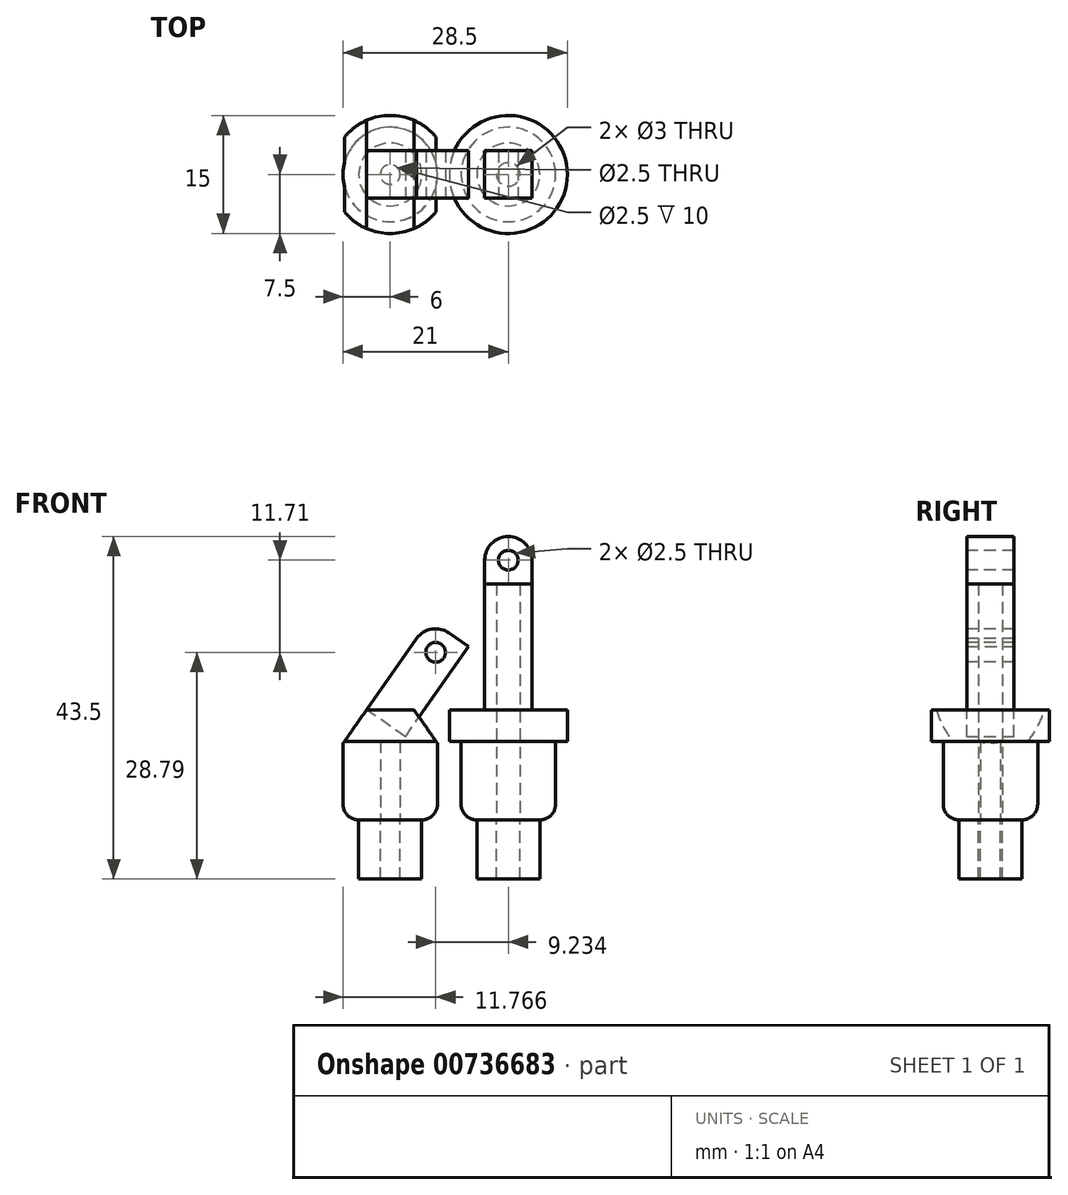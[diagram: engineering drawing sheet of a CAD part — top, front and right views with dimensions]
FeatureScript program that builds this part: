
annotation { "Feature Type Name" : "Feature", "Feature Type Description" : "" }
export const myFeature = defineFeature(function(context is Context, id is Id, definition is map)
    precondition{}
    {
        {
            var Q0;
            Q0=qCreatedBy(makeId("Top.planeOp"),FACE);
            var sketch = newSketch(context, id + "F0", { "sketchPlane" : qUnion([Q0])});
            skCircle(sketch, "E0", {"center": v(0, 0) * mm, "radius": 6 * mm});
            skCircle(sketch, "E1", {"center": v(15, 0) * mm, "radius": 6 * mm});
            skCircle(sketch, "E2", {"center": v(15, 0) * mm, "radius": 1.5 * mm});
            skSolve(sketch);
        }
        {
            var Q0;
            Q0=makeQuery(id+"F0.imprint","IMPRINT",FACE,{"disambiguationData":[TD([[makeQuery(id+"F0.imprint","IMPRINT",EDGE,{"derivedFrom":sQuery(id+"F0.wireOp",EDGE,"E0")}),1.0]])]});
            extrude(context, id + "F1", {"entities" : qUnion([Q0]), "depth" : 10 * mm, "offsetDistance" : 25 * mm});
        }
        {
            var Q0;
            Q0=makeQuery(id+"F1.opExtrude","CAP_FACE",FACE,{"disambiguationData":[OSD([sQuery(id+"F0.wireOp",EDGE,"E0")])],"isStart":false});
            var sketch = newSketch(context, id + "F2", { "sketchPlane" : qUnion([Q0])});
            skCircle(sketch, "E3", {"center": v(0, 0) * mm, "radius": 7.5 * mm});
            skSolve(sketch);
        }
        {
            var Q0;
            Q0 = qSketchRegion(id + "F2", true);
            extrude(context, id + "F3", {"entities" : qUnion([Q0]), "operationType" : NewBodyOperationType.ADD, "depth" : 4 * mm, "offsetDistance" : 25 * mm});
        }
        {
            var Q0;
            Q0=makeQuery(id+"F3.opExtrude","CAP_FACE",FACE,{"disambiguationData":[OSD([sQuery(id+"F2.wireOp",EDGE,"E3")])],"isStart":false});
            var sketch = newSketch(context, id + "F4", { "sketchPlane" : qUnion([Q0])});
            skLineSegment(sketch, "E4.bottom", {"start": v(3, 6.87) * mm, "end": v(10, 6.87) * mm});
            skLineSegment(sketch, "E4.top", {"start": v(3, -6.87) * mm, "end": v(10, -6.87) * mm});
            skLineSegment(sketch, "E4.right", {"start": v(10, 6.87) * mm, "end": v(10, -6.87) * mm});
            skLineSegment(sketch, "E5.bottom", {"start": v(-3, 6.87) * mm, "end": v(-10, 6.87) * mm});
            skLineSegment(sketch, "E5.top", {"start": v(-3, -6.87) * mm, "end": v(-10, -6.87) * mm});
            skLineSegment(sketch, "E5.left", {"start": v(-3, 6.87) * mm, "end": v(-3, -6.87) * mm});
            skLineSegment(sketch, "E5.right", {"start": v(-10, 6.87) * mm, "end": v(-10, -6.87) * mm});
            skLineSegment(sketch, "E6", {"start": v(3, -6.87) * mm, "end": v(3, 6.87) * mm});
            skLineSegment(sketch, "E7.top", {"start": v(-3, -3) * mm, "end": v(3, -3) * mm});
            skLineSegment(sketch, "E7.left", {"start": v(-3, 0) * mm, "end": v(-3, -3) * mm});
            skLineSegment(sketch, "E7.right", {"start": v(3, 3) * mm, "end": v(3, -3) * mm});
            skLineSegment(sketch, "E8", {"start": v(3, 3) * mm, "end": v(-3, 3) * mm});
            skLineSegment(sketch, "E9", {"start": v(-3, 3) * mm, "end": v(-3, 0) * mm});
            skSolve(sketch);
        }
        {
            var Q0;
            {var subQ0=sQuery(id+"F4.wireOp",EDGE,"E5.bottom");Q0=makeQuery(id+"F4.imprint","IMPRINT",FACE,{"disambiguationData":[TD([[makeQuery(id+"F4.imprint","IMPRINT",EDGE,{"derivedFrom":subQ0}),1.0]])]});}
            var Q1;
            {var subQ0=sQuery(id+"F4.wireOp",EDGE,"E5.left");var subQ1=makeQuery(id+"F4.imprint","INTERSECT",VERTEX,{"derivedFrom":[sQuery(id+"F4.wireOp",EDGE,"yuGE9SbZ-14rk-lHCZ-kvU9-YbVtqfjyu9ov.bottom"),subQ0]});Q1=makeQuery(id+"F4.imprint","IMPRINT",FACE,{"disambiguationData":[TD([[makeQuery(id+"F4.imprint","IMPRINT",EDGE,{"disambiguationData":[TD([[subQ1,-1.0]])],"derivedFrom":subQ0}),-1.0]])]});}
            var Q2;
            Q2=sQuery(id+"F4.wireOp",EDGE,"E5.left");
            revolve(context, id + "F5", {"operationType" : NewBodyOperationType.REMOVE, "surfaceOperationType" : NewSurfaceOperationType.NEW, "entities" : qUnion([Q0, Q1]), "axis" : qUnion([Q2]), "revolveType" : RevolveType.ONE_DIRECTION, "angle" : 55 * degree});
        }
        {
            var Q0;
            {var subQ0=sQuery(id+"F4.wireOp",EDGE,"E6");Q0=makeQuery(id+"F4.imprint","IMPRINT",FACE,{"disambiguationData":[TD([[makeQuery(id+"F4.imprint","IMPRINT",EDGE,{"derivedFrom":subQ0}),-1.0]])]});}
            var Q1;
            {var subQ0=sQuery(id+"F4.wireOp",EDGE,"E4.bottom");Q1=makeQuery(id+"F4.imprint","IMPRINT",FACE,{"disambiguationData":[TD([[makeQuery(id+"F4.imprint","IMPRINT",EDGE,{"derivedFrom":subQ0}),-1.0]])]});}
            var Q2;
            Q2=sQuery(id+"F4.wireOp",EDGE,"E6");
            revolve(context, id + "F6", {"operationType" : NewBodyOperationType.REMOVE, "surfaceOperationType" : NewSurfaceOperationType.NEW, "entities" : qUnion([Q0, Q1]), "axis" : qUnion([Q2]), "revolveType" : RevolveType.ONE_DIRECTION, "angle" : 55 * degree});
        }
        {
            var Q0;
            Q0=makeQuery(id+"F1.opExtrude","CAP_FACE",FACE,{"disambiguationData":[OSD([sQuery(id+"F0.wireOp",EDGE,"E0")])],"isStart":true});
            var sketch = newSketch(context, id + "F7", { "sketchPlane" : qUnion([Q0])});
            skCircle(sketch, "E10", {"center": v(0, 0) * mm, "radius": 1.25 * mm});
            skSolve(sketch);
        }
        {
            var Q0;
            Q0 = qSketchRegion(id + "F7", true);
            extrude(context, id + "F8", {"entities" : qUnion([Q0]), "operationType" : NewBodyOperationType.REMOVE, "oppositeDirection" : true, "depth" : 10 * mm, "offsetDistance" : 25 * mm});
        }
        {
            var Q0;
            Q0=makeQuery(id+"F1.opExtrude","CAP_EDGE",EDGE,{"disambiguationData":[OSD([sQuery(id+"F0.wireOp",EDGE,"E0")])],"isStart":true});
            fillet(context, id + "F9", {"entities" : qUnion([Q0]), "radius" : 2 * mm, "tangentPropagation" : true, "allowEdgeOverflow" : false});
        }
        {
            var Q0;
            Q0=makeQuery(id+"F0.imprint","IMPRINT",FACE,{"disambiguationData":[TD([[makeQuery(id+"F0.imprint","IMPRINT",EDGE,{"derivedFrom":sQuery(id+"F0.wireOp",EDGE,"E1")}),1.0]])]});
            extrude(context, id + "F10", {"entities" : qUnion([Q0]), "depth" : 10 * mm, "offsetDistance" : 25 * mm});
        }
        {
            var Q0;
            Q0=makeQuery(id+"F10.opExtrude","CAP_FACE",FACE,{"disambiguationData":[OSD([sQuery(id+"F0.wireOp",EDGE,"E1")])],"isStart":false});
            var sketch = newSketch(context, id + "F11", { "sketchPlane" : qUnion([Q0])});
            skCircle(sketch, "E11", {"center": v(15, 0) * mm, "radius": 7.5 * mm});
            skSolve(sketch);
        }
        {
            var Q0;
            Q0 = qSketchRegion(id + "F11", true);
            extrude(context, id + "F12", {"entities" : qUnion([Q0]), "operationType" : NewBodyOperationType.ADD, "depth" : 4 * mm, "offsetDistance" : 25 * mm});
        }
        {
            var Q0;
            Q0=makeQuery(id+"F10.opExtrude","CAP_EDGE",EDGE,{"disambiguationData":[OSD([sQuery(id+"F0.wireOp",EDGE,"E1")])],"isStart":true});
            fillet(context, id + "F13", {"entities" : qUnion([Q0]), "radius" : 2 * mm, "tangentPropagation" : true, "allowEdgeOverflow" : false});
        }
        {
            var Q0;
            Q0=makeQuery(id+"F12.boolean.opBoolean","SPLIT",FACE,{"disambiguationData":[TD([makeQuery(id+"F10.opExtrude","SWEPT_FACE",FACE,{"disambiguationData":[OSD([sQuery(id+"F0.wireOp",EDGE,"E2")])]})])],"derivedFrom":makeQuery(id+"F12.opExtrude","CAP_FACE",FACE,{"disambiguationData":[OSD([sQuery(id+"F11.wireOp",EDGE,"E11")])],"isStart":true})});
            extrude(context, id + "F14", {"entities" : qUnion([Q0]), "operationType" : NewBodyOperationType.REMOVE, "oppositeDirection" : true, "depth" : 25 * mm, "offsetDistance" : 25 * mm});
        }
        {
            var Q0;
            Q0=makeQuery(id+"F5.boolean.opBoolean","COPY",FACE,{"derivedFrom":makeQuery(id+"F5.opRevolve","CAP_FACE",FACE,{"disambiguationData":[OSD([sQuery(id+"F4.wireOp",EDGE,"E5.bottom"),sQuery(id+"F4.wireOp",EDGE,"E5.top"),sQuery(id+"F4.wireOp",EDGE,"E5.left"),sQuery(id+"F4.wireOp",EDGE,"E5.right"),sQuery(id+"F4.wireOp",EDGE,"E7.left"),sQuery(id+"F4.wireOp",EDGE,"E9")])],"isStart":false})});
            var sketch = newSketch(context, id + "F15", { "sketchPlane" : qUnion([Q0])});
            skLineSegment(sketch, "E12.bottom", {"start": v(3, 9.75) * mm, "end": v(-3, 9.75) * mm});
            skLineSegment(sketch, "E12.top", {"start": v(3, 23.75) * mm, "end": v(-3, 23.75) * mm});
            skLineSegment(sketch, "E12.left", {"start": v(3, 9.75) * mm, "end": v(3, 23.75) * mm});
            skLineSegment(sketch, "E12.right", {"start": v(-3, 9.75) * mm, "end": v(-3, 23.75) * mm});
            skSolve(sketch);
        }
        {
            var Q0;
            Q0=makeQuery(id+"F15.imprint","IMPRINT",FACE,{"disambiguationData":[TD([[makeQuery(id+"F15.imprint","IMPRINT",EDGE,{"derivedFrom":sQuery(id+"F15.wireOp",EDGE,"E12.bottom")}),1.0]])]});
            extrude(context, id + "F16", {"entities" : qUnion([Q0]), "oppositeDirection" : true, "depth" : 6 * mm, "offsetDistance" : 25 * mm});
        }
        {
            var Q0;
            Q0=makeQuery(id+"F16.opExtrude","SWEPT_FACE",FACE,{"disambiguationData":[OSD([sQuery(id+"F15.wireOp",EDGE,"E12.left")])]});
            var sketch = newSketch(context, id + "F17", { "sketchPlane" : qUnion([Q0])});
            skCircle(sketch, "E13", {"center": v(5.77, 21.29) * mm, "radius": 3 * mm});
            skPoint(sketch, "E13.first.point", {"position": v(7.49, 23.75) * mm});
            skPoint(sketch, "E13.second.point", {"position": v(3.26, 22.94) * mm});
            skPoint(sketch, "E13.third.point", {"position": v(8.24, 19.6) * mm});
            skCircle(sketch, "E14", {"center": v(5.77, 21.29) * mm, "radius": 1.25 * mm});
            skSolve(sketch);
        }
        {
            var Q0;
            {var subQ0=sQuery(id+"F17.wireOp",EDGE,"E13");var subQ1=sQuery(id+"F15.wireOp",EDGE,"E12.left");var subQ2=makeQuery(id+"F16.opExtrude","CAP_EDGE",EDGE,{"disambiguationData":[OSD([subQ1])],"isStart":true});var subQ3=makeQuery(id+"F17.imprint","INTERSECT",VERTEX,{"disambiguationData":[OD(0.0)],"derivedFrom":[subQ2,subQ0]});Q0=makeQuery(id+"F17.imprint","IMPRINT",FACE,{"disambiguationData":[TD([[makeQuery(id+"F17.imprint","IMPRINT",EDGE,{"disambiguationData":[TD([[subQ3,1.0]])],"derivedFrom":subQ0}),-1.0]])]});}
            var Q1;
            {var subQ0=sQuery(id+"F17.wireOp",EDGE,"E13");var subQ1=sQuery(id+"F15.wireOp",EDGE,"E12.left");var subQ4=makeQuery(id+"F16.opExtrude","CAP_EDGE",EDGE,{"disambiguationData":[OSD([subQ1])],"isStart":false});var subQ5=makeQuery(id+"F17.imprint","INTERSECT",VERTEX,{"disambiguationData":[OD(1.0)],"derivedFrom":[subQ4,subQ0]});Q1=makeQuery(id+"F17.imprint","IMPRINT",FACE,{"disambiguationData":[TD([[makeQuery(id+"F17.imprint","IMPRINT",EDGE,{"disambiguationData":[TD([[subQ5,-1.0]])],"derivedFrom":subQ0}),-1.0]])]});}
            var Q2;
            Q2=makeQuery(id+"F17.imprint","IMPRINT",FACE,{"disambiguationData":[TD([[makeQuery(id+"F17.imprint","IMPRINT",EDGE,{"derivedFrom":sQuery(id+"F17.wireOp",EDGE,"E14")}),1.0]])]});
            extrude(context, id + "F18", {"entities" : qUnion([Q0, Q1, Q2]), "operationType" : NewBodyOperationType.REMOVE, "oppositeDirection" : true, "depth" : 25 * mm, "offsetDistance" : 25 * mm});
        }
        {
            var Q0;
            Q0=makeQuery(id+"F1.opExtrude","CAP_FACE",FACE,{"disambiguationData":[OSD([sQuery(id+"F0.wireOp",EDGE,"E0")])],"isStart":true});
            var Q1;
            Q1=makeQuery(id+"F10.opExtrude","CAP_FACE",FACE,{"disambiguationData":[OSD([sQuery(id+"F0.wireOp",EDGE,"E1"),sQuery(id+"F0.wireOp",EDGE,"E2")])],"isStart":true});
            extrude(context, id + "F19", {"entities" : qUnion([Q0, Q1]), "depth" : 7.5 * mm, "offsetDistance" : 25 * mm});
        }
        {
            var Q0;
            Q0=makeQuery(id+"F12.opExtrude","CAP_FACE",FACE,{"disambiguationData":[OSD([sQuery(id+"F11.wireOp",EDGE,"E11")])],"isStart":false});
            var sketch = newSketch(context, id + "F20", { "sketchPlane" : qUnion([Q0])});
            skLineSegment(sketch, "E15.bottom", {"start": v(12, -3) * mm, "end": v(18, -3) * mm});
            skLineSegment(sketch, "E15.top", {"start": v(12, 3) * mm, "end": v(18, 3) * mm});
            skLineSegment(sketch, "E15.left", {"start": v(12, -3) * mm, "end": v(12, 3) * mm});
            skLineSegment(sketch, "E15.right", {"start": v(18, -3) * mm, "end": v(18, 3) * mm});
            skSolve(sketch);
        }
        {
            var Q0;
            Q0=makeQuery(id+"F20.imprint","IMPRINT",FACE,{"disambiguationData":[TD([[makeQuery(id+"F20.imprint","IMPRINT",EDGE,{"derivedFrom":sQuery(id+"F20.wireOp",EDGE,"E15.bottom")}),1.0]])]});
            extrude(context, id + "F21", {"entities" : qUnion([Q0]), "operationType" : NewBodyOperationType.ADD, "depth" : 10 * mm, "offsetDistance" : 25 * mm});
        }
        {
            var Q0;
            Q0=makeQuery(id+"F21.opExtrude","CAP_FACE",FACE,{"disambiguationData":[OSD([sQuery(id+"F0.wireOp",EDGE,"E2"),sQuery(id+"F11.wireOp",EDGE,"E11"),sQuery(id+"F20.wireOp",EDGE,"E15.bottom"),sQuery(id+"F20.wireOp",EDGE,"E15.top"),sQuery(id+"F20.wireOp",EDGE,"E15.left"),sQuery(id+"F20.wireOp",EDGE,"E15.right")])],"isStart":false});
            extrude(context, id + "F22", {"entities" : qUnion([Q0]), "operationType" : NewBodyOperationType.ADD, "depth" : 6 * mm, "offsetDistance" : 25 * mm});
        }
        {
            var Q0;
            Q0=makeQuery(id+"F22.opExtrude","CAP_FACE",FACE,{"disambiguationData":[OSD([sQuery(id+"F0.wireOp",EDGE,"E2"),sQuery(id+"F11.wireOp",EDGE,"E11"),sQuery(id+"F20.wireOp",EDGE,"E15.bottom"),sQuery(id+"F20.wireOp",EDGE,"E15.top"),sQuery(id+"F20.wireOp",EDGE,"E15.left"),sQuery(id+"F20.wireOp",EDGE,"E15.right")])],"isStart":false});
            var sketch = newSketch(context, id + "F23", { "sketchPlane" : qUnion([Q0])});
            skLineSegment(sketch, "E16.bottom", {"start": v(12, 3) * mm, "end": v(18, 3) * mm});
            skLineSegment(sketch, "E16.top", {"start": v(12, -3) * mm, "end": v(18, -3) * mm});
            skLineSegment(sketch, "E16.left", {"start": v(12, 3) * mm, "end": v(12, -3) * mm});
            skLineSegment(sketch, "E16.right", {"start": v(18, 3) * mm, "end": v(18, -3) * mm});
            skSolve(sketch);
        }
        {
            var Q0;
            Q0 = qSketchRegion(id + "F23", true);
            extrude(context, id + "F24", {"entities" : qUnion([Q0]), "depth" : 6 * mm, "offsetDistance" : 25 * mm});
        }
        {
            var Q0;
            Q0=makeQuery(id+"F24.opExtrude","SWEPT_FACE",FACE,{"disambiguationData":[OSD([sQuery(id+"F23.wireOp",EDGE,"E16.top")])]});
            var sketch = newSketch(context, id + "F25", { "sketchPlane" : qUnion([Q0])});
            skCircle(sketch, "E17", {"center": v(15, 33) * mm, "radius": 3 * mm});
            skPoint(sketch, "E17.centerSnap0", {"position": v(12, 33) * mm});
            skPoint(sketch, "E17.centerSnap1", {"position": v(15, 36) * mm});
            skCircle(sketch, "E18", {"center": v(15, 33) * mm, "radius": 1.25 * mm});
            skSolve(sketch);
        }
        {
            var Q0;
            {var subQ0=sQuery(id+"F25.wireOp",EDGE,"E17");var subQ1=sQuery(id+"F23.wireOp",EDGE,"E16.top");var subQ2=makeQuery(id+"F24.opExtrude","CAP_EDGE",EDGE,{"disambiguationData":[OSD([subQ1])],"isStart":false});var subQ3=makeQuery(id+"F25.imprint","INTERSECT",VERTEX,{"derivedFrom":[subQ2,subQ0]});Q0=makeQuery(id+"F25.imprint","IMPRINT",FACE,{"disambiguationData":[TD([[makeQuery(id+"F25.imprint","IMPRINT",EDGE,{"disambiguationData":[TD([[subQ3,-1.0]])],"derivedFrom":subQ0}),-1.0]])]});}
            var Q1;
            {var subQ0=sQuery(id+"F25.wireOp",EDGE,"E17");var subQ1=sQuery(id+"F23.wireOp",EDGE,"E16.top");var subQ2=makeQuery(id+"F24.opExtrude","CAP_EDGE",EDGE,{"disambiguationData":[OSD([subQ1])],"isStart":false});var subQ3=makeQuery(id+"F25.imprint","INTERSECT",VERTEX,{"derivedFrom":[subQ2,subQ0]});Q1=makeQuery(id+"F25.imprint","IMPRINT",FACE,{"disambiguationData":[TD([[makeQuery(id+"F25.imprint","IMPRINT",EDGE,{"disambiguationData":[TD([[subQ3,1.0]])],"derivedFrom":subQ0}),-1.0]])]});}
            var Q2;
            Q2=makeQuery(id+"F25.imprint","IMPRINT",FACE,{"disambiguationData":[TD([[makeQuery(id+"F25.imprint","IMPRINT",EDGE,{"derivedFrom":sQuery(id+"F25.wireOp",EDGE,"E18")}),1.0]])]});
            extrude(context, id + "F26", {"entities" : qUnion([Q0, Q1, Q2]), "operationType" : NewBodyOperationType.REMOVE, "oppositeDirection" : true, "depth" : 25 * mm, "offsetDistance" : 25 * mm});
        }
    });
